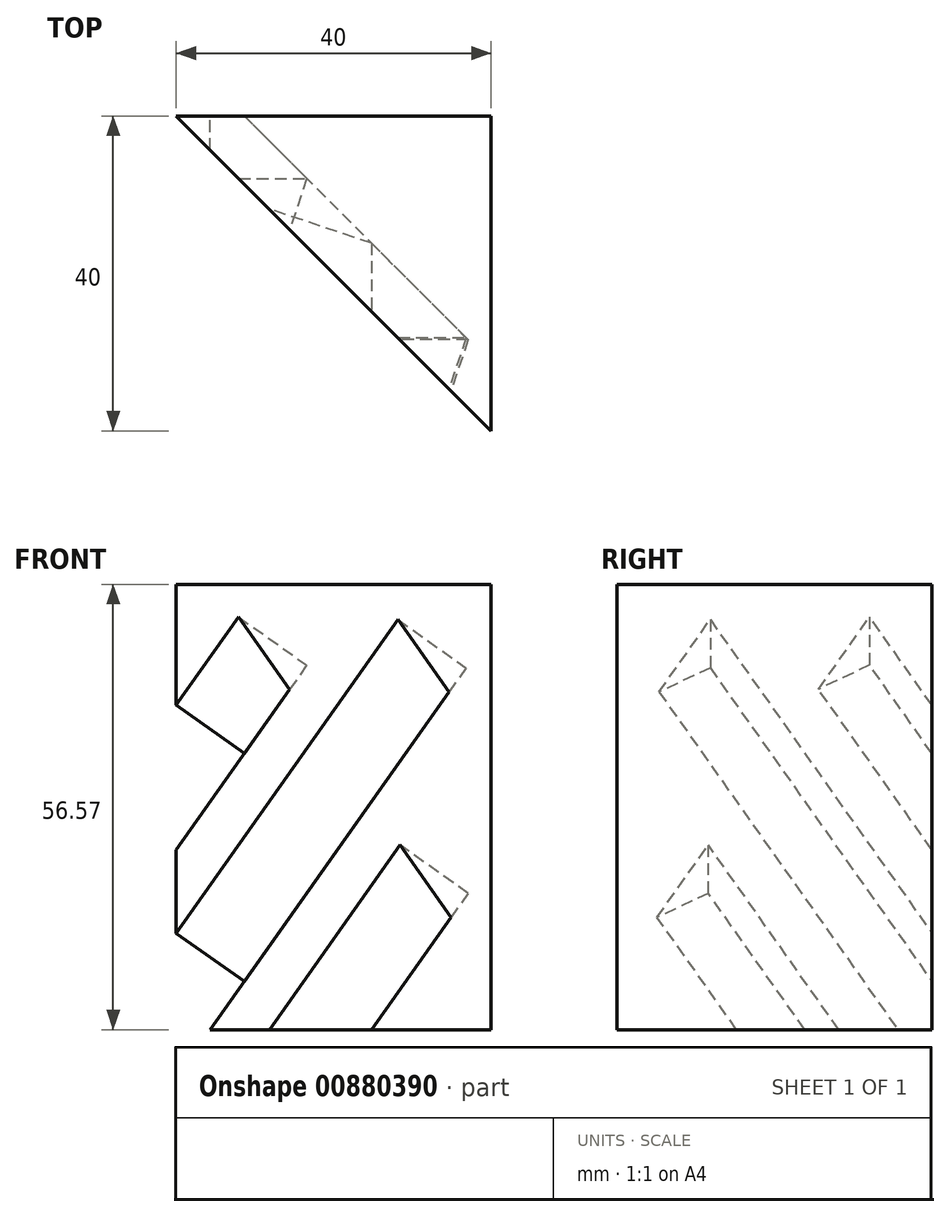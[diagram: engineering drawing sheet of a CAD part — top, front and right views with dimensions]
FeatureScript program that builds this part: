
annotation { "Feature Type Name" : "Feature", "Feature Type Description" : "" }
export const myFeature = defineFeature(function(context is Context, id is Id, definition is map)
    precondition{}
    {
        {
            var Q0;
            Q0=qCreatedBy(makeId("Top.planeOp"),FACE);
            var sketch = newSketch(context, id + "F0", { "sketchPlane" : qUnion([Q0])});
            skLineSegment(sketch, "E0.bottom", {"start": v(20, 20) * mm, "end": v(-20, 20) * mm});
            skLineSegment(sketch, "E0.top", {"start": v(20, -20) * mm, "end": v(-20, -20) * mm});
            skLineSegment(sketch, "E0.left", {"start": v(20, 20) * mm, "end": v(20, -20) * mm});
            skLineSegment(sketch, "E0.right", {"start": v(-20, 20) * mm, "end": v(-20, -20) * mm});
            skPoint(sketch, "E0.middle", {"position": v(0, 0) * mm});
            skLineSegment(sketch, "E1", {"start": v(-20, 20) * mm, "end": v(20, -20) * mm});
            skSolve(sketch);
        }
        {
            var Q0;
            Q0=makeQuery(id+"F0.imprint","IMPRINT",FACE,{"disambiguationData":[TD([[makeQuery(id+"F0.imprint","IMPRINT",EDGE,{"derivedFrom":sQuery(id+"F0.wireOp",EDGE,"E0.bottom")}),1.0]])]});
            extrude(context, id + "F1", {"entities" : qUnion([Q0]), "depth" : (40 * sqrt(2)) * mm, "offsetDistance" : 25 * mm});
        }
        {
            var Q0;
            Q0=makeQuery(id+"F1.opExtrude","SWEPT_FACE",FACE,{"disambiguationData":[OSD([sQuery(id+"F0.wireOp",EDGE,"E1")])]});
            var sketch = newSketch(context, id + "F2", { "sketchPlane" : qUnion([Q0])});
            skLineSegment(sketch, "E2", {"start": v(28.28, 0) * mm, "end": v(-28.28, 56.57) * mm});
            skSolve(sketch);
        }
        {
            var Q0;
            Q0=sQuery(id+"F2.wireOp",EDGE,"E2");
            var Q1;
            Q1=makeQuery(id+"F2.imprint","IMPRINT",FACE,{"disambiguationData":[TD([[makeQuery(id+"F2.imprint","IMPRINT",EDGE,{"derivedFrom":sQuery(id+"F2.wireOp",EDGE,"E2")}),-1.0]])]});
            cPlane(context, id + "F3", {"entities" : qUnion([Q0, Q1]), "cplaneType" : CPlaneType.LINE_ANGLE, "offset" : 25 * mm, "angle" : 90 * degree, "width" : 150 * mm, "height" : 150 * mm});
        }
        {
            var Q0;
            Q0=qCreatedBy(id+"F3.planeOp",FACE);
            var sketch = newSketch(context, id + "F4", { "sketchPlane" : qUnion([Q0])});
            skLineSegment(sketch, "E3", {"start": v(-28.38, -40.13) * mm, "end": v(-28.38, -29.52) * mm});
            skLineSegment(sketch, "E4", {"start": v(-28.38, -29.52) * mm, "end": v(-20.88, -29.52) * mm});
            skLineSegment(sketch, "E5", {"start": v(-20.88, -29.52) * mm, "end": v(-16.55, -23.4) * mm});
            skLineSegment(sketch, "E6", {"start": v(-16.55, -23.4) * mm, "end": v(-16.55, -12.8) * mm});
            skLineSegment(sketch, "E7", {"start": v(-16.55, -12.8) * mm, "end": v(-9.05, -12.8) * mm});
            skLineSegment(sketch, "E8", {"start": v(-4.72, 3.94) * mm, "end": v(2.78, 3.94) * mm});
            skLineSegment(sketch, "E9", {"start": v(-34.64, -48.99) * mm, "end": v(-28.38, -40.13) * mm});
            skLineSegment(sketch, "E10", {"start": v(2.78, 3.94) * mm, "end": v(11.55, 16.33) * mm});
            skLineSegment(sketch, "E11", {"start": v(-4.72, 3.94) * mm, "end": v(-4.72, -6.67) * mm});
            skLineSegment(sketch, "E12", {"start": v(-4.72, -6.67) * mm, "end": v(-9.05, -12.8) * mm});
            skLineSegment(sketch, "E13.0", {"start": v(11.55, 16.33) * mm, "end": v(-34.64, -48.99) * mm});
            skLineSegment(sketch, "E14", {"start": v(-16.55, -12.8) * mm, "end": v(-11.55, -16.33) * mm});
            skLineSegment(sketch, "E15.MirrorCS", {"start": v(5.28, -3.14) * mm, "end": v(-4.72, -6.67) * mm});
            skLineSegment(sketch, "E16.MirrorCS", {"start": v(5.28, -3.14) * mm, "end": v(2.78, 3.94) * mm});
            skLineSegment(sketch, "E17.MirrorCS", {"start": v(-6.55, -19.87) * mm, "end": v(-9.05, -12.8) * mm});
            skLineSegment(sketch, "E18.MirrorCS", {"start": v(-16.55, -23.4) * mm, "end": v(-6.55, -19.87) * mm});
            skLineSegment(sketch, "E19.MirrorCS", {"start": v(-18.38, -36.6) * mm, "end": v(-20.88, -29.52) * mm});
            skLineSegment(sketch, "E20.MirrorCS", {"start": v(-28.38, -40.13) * mm, "end": v(-18.38, -36.6) * mm});
            skSolve(sketch);
        }
        {
            var Q0;
            Q0=makeQuery(id+"F1.opExtrude","SWEPT_FACE",FACE,{"disambiguationData":[OSD([sQuery(id+"F0.wireOp",EDGE,"E1")])]});
            var sketch = newSketch(context, id + "F5", { "sketchPlane" : qUnion([Q0])});
            skLineSegment(sketch, "E21", {"start": v(-28.28, 56.57) * mm, "end": v(28.28, 0) * mm});
            skLineSegment(sketch, "E22", {"start": v(28.28, 0) * mm, "end": v(-28.28, 0) * mm});
            skLineSegment(sketch, "E23", {"start": v(-28.28, 0) * mm, "end": v(-28.28, 56.57) * mm});
            skLineSegment(sketch, "E24", {"start": v(-28.28, 56.57) * mm, "end": v(28.28, 56.57) * mm});
            skLineSegment(sketch, "E25", {"start": v(28.28, 56.57) * mm, "end": v(28.28, 0) * mm});
            skSolve(sketch);
        }
        {
            var Q0;
            {var subQ2=sQuery(id+"F4.wireOp",EDGE,"E19.MirrorCS");Q0=makeQuery(id+"F4.imprint","IMPRINT",FACE,{"disambiguationData":[TD([[makeQuery(id+"F4.imprint","IMPRINT",EDGE,{"derivedFrom":subQ2}),1.0]])]});}
            var Q1;
            {var subQ2=sQuery(id+"F4.wireOp",EDGE,"E15.MirrorCS");Q1=makeQuery(id+"F4.imprint","IMPRINT",FACE,{"disambiguationData":[TD([[makeQuery(id+"F4.imprint","IMPRINT",EDGE,{"derivedFrom":subQ2}),-1.0]])]});}
            extrude(context, id + "F6", {"entities" : qUnion([Q0, Q1]), "operationType" : NewBodyOperationType.REMOVE, "depth" : 50 * mm, "offsetDistance" : 25 * mm, "hasSecondDirection" : true, "secondDirectionOppositeDirection" : true, "secondDirectionDepth" : 5 * mm});
        }
        {
            var Q0;
            {var subQ0=sQuery(id+"F4.wireOp",EDGE,"E17.MirrorCS");Q0=makeQuery(id+"F4.imprint","IMPRINT",FACE,{"disambiguationData":[TD([[makeQuery(id+"F4.imprint","IMPRINT",EDGE,{"derivedFrom":subQ0}),1.0]])]});}
            extrude(context, id + "F7", {"entities" : qUnion([Q0]), "operationType" : NewBodyOperationType.REMOVE, "oppositeDirection" : true, "depth" : 25 * mm, "offsetDistance" : 25 * mm, "hasSecondDirection" : true, "secondDirectionOppositeDirection" : false, "secondDirectionDepth" : 50 * mm});
        }
    });
